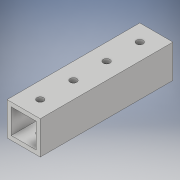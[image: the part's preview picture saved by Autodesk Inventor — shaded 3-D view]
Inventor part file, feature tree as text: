
AUTODESK INVENTOR PART (.ipt)
format: ipt  version: 2018 (Build 220112000, 112)  size: 116,224 bytes
history: native  units: in
note: dims shown in document units (in); Inventor stores cm internally (conversion verified against a paired STEP export)
features: extrude x2, sketch x2
ambient origin geometry x8: Origin, YZ Plane, XZ Plane, XY Plane, X Axis, Y Axis, Z Axis, Center Point
bodies: Solid1 (feature_tree)
feature tree (4):
  extrude  "Extrusion1"  Depth=1.0in
  extrude  "Extrusion2"  Depth=4.0in TaperAngle=0.0deg
  sketch  "Sketch1"  dims[d0=1.0in d1=1.0in]
  sketch  "Sketch2"  dims[d2=0.125in d3=4.0in d4=0.0in d5=0.5in d6=1.0in d7=1.0in d8=1.0in d9=0.2031in d10=4.0in d11=0.0in]
